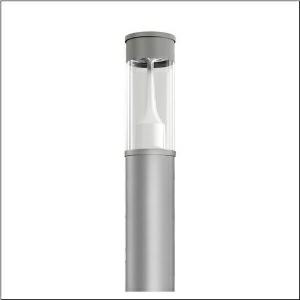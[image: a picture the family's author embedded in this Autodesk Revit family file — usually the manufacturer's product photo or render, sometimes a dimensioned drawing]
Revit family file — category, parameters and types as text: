
# Revit family: city-light_400_iq___p1_0a_5xa5305bf14hp_df67
name_source: partatom
category: Lighting Fixtures
units: mm (PartAtom-declared; Revit-internal decimal feet)

## family parameters
Cut with Voids When Loaded = No
Host = Face
Light Source = No
Part Type = Normal
Room Calculation Point = No
Round Connector Dimension = Use Diameter
Shared = No

## types (1)
- --- (1 x LED, 3890 lm, 33.6 W, 2200K)
    Apparent Load = 34 VA
    CIE Flux Codes = 31 62 91 95 100
    Color Rendering = 70
    Color Temperature = 2200K
    Default Elevation = 1800 mm
    Description = City-Light 400 iQ, light pillar, Module 540 iQ-SR, primary light control with 3 zone facetted reflector, of plastic, silver coated, highly specular, structured, primary optical cover: cover, of PMMA, transparent, partly coated, light distribution: P1.0a, primary light characteristic: strongly asymmetric, LED, High Power LED, rated luminous flux: 3.890lm, luminous efficacy: 116lm/W, light colour: 722, colour temperature: 2200K, control gear: iQ Street-Remote, control: pre-setting: logarithmic dimming characteristic, Street-Remote, Auto-Match, Temp-Guard, Lumen-Switch, Night-Set, Smart-Wire, Light-Fading, Desk-Remote (wireless, voltage-free reading and setting of iQ features in the workshop via application-optimized NFC function/RFID function), optimised constant luminous flux control (CLO 2.0), with terminal, 6-pole, max. 2.5mm², mains connection: 230..240V, AC, 50/60Hz, start of lifetime: 34W, end of service life: 36W, reduction: 15W, luminaire housing, cylindrical, of extruded aluminium section, coated, Siteco® metallic grey (DB 702S), length: 4.694mm, diameter: 200mm, Module 540 iQ-SR, traffic white (RAL 9016), equipment: Power, protection rating (complete): IP65, insulation class (complete): insulation class II (safety insulation), certification: CE, ENEC, VDE, packaging unit: 1 piece

Light Distribution: P1.0a
    Height = 500 mm
    Lamp = 1 x LED
    Lamp Light Flux = 3890 lm
    Lamp Power = 33.6 W
    Lamp count = 1
    Length = 200 mm  [stored 0.656168 ft]
    Luminous efficacy = 116 lm/W
    Manufacturer = Siteco
    ModVariant = No
    Model = 5XA5305BF14HP
    Mounting Place = Floor
    Mounting Type = Freestanding
    Number of Poles = 1
    OnlyDefault = Yes
    Power Factor = 1
    Product Name = City-Light 400 iQ | P1.0a
    Product group = light pillar
    ProductGroupID = 1301
    Protection Class = Protection class II
    Protection Degree = IP 65
    RLX_Detail_Level = 1
    RLX_Emergency_Light_Flux = 0 lm
    RLX_Emergency_Type = 0
    RLX_Emergency_Type_DB = No
    RlxData = <blob elided: 53845 chars, md5=4394231c>
    Socket = socket
    Standby Power = 0 W
    System Light Flux = 3890 lm
    System Power = 34 W
    Type Comments = factory setting: luminous flux: 100 % | dim-lin: 254 | 695 mA
    Type Image = l_1006916.jpg
    URL = http://relux.com
    VarID = @adj_214085
    Voltage = 0 V
    Weight = 0.00 kg
    Width = 0 mm  [stored 0 ft]

note: [stored X ft] marks values corroborated as IEEE doubles in the binary element streams (Revit-internal decimal feet)

## geometry (parser evidence)
native form markers: Blend x4, Sweep x13
no freeform markers — native parametric forms only
